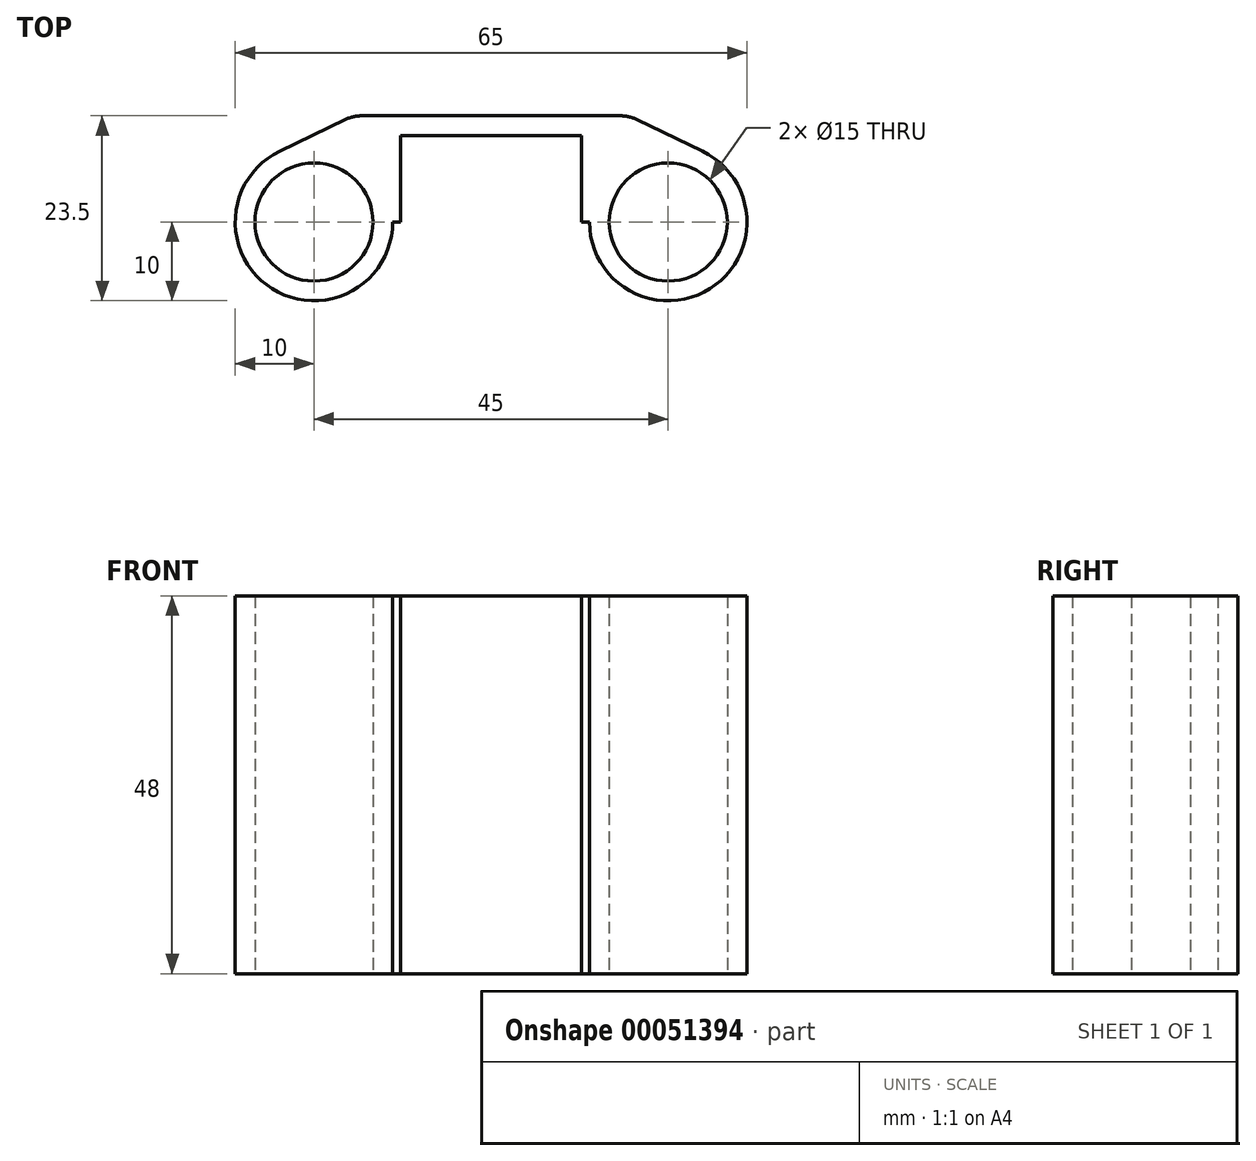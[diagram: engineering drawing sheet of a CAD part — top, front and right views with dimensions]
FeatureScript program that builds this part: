
annotation { "Feature Type Name" : "Feature", "Feature Type Description" : "" }
export const myFeature = defineFeature(function(context is Context, id is Id, definition is map)
    precondition{}
    {
        {
            var Q0;
            Q0=qCreatedBy(makeId("Top.planeOp"),FACE);
            var sketch = newSketch(context, id + "F0", { "sketchPlane" : qUnion([Q0])});
            skCircle(sketch, "E0", {"center": v(22.5, 0) * mm, "radius": 7.5 * mm});
            skCircle(sketch, "E1", {"center": v(-22.5, 0) * mm, "radius": 7.5 * mm});
            skLineSegment(sketch, "E2", {"start": v(-22.5, 0) * mm, "end": v(22.5, 0) * mm, "construction": true});
            skArc(sketch, "E3", {"start": v(-26.83, 9.01) * mm, "mid": v(-27.82, -8.47) * mm, "end": v(-12.5, 0) * mm});
            skArc(sketch, "E4", {"start": v(12.5, 0) * mm, "mid": v(27.82, -8.47) * mm, "end": v(26.83, 9.01) * mm});
            skLineSegment(sketch, "E5", {"start": v(0, 0) * mm, "end": v(0, 13.5) * mm, "construction": true});
            skLineSegment(sketch, "E6.bottom", {"start": v(10, 10) * mm, "end": v(-10, 10) * mm, "construction": true});
            skLineSegment(sketch, "E6.top", {"start": v(10, -10) * mm, "end": v(-10, -10) * mm, "construction": true});
            skLineSegment(sketch, "E6.left", {"start": v(10, 10) * mm, "end": v(10, -10) * mm, "construction": true});
            skLineSegment(sketch, "E6.right", {"start": v(-10, 10) * mm, "end": v(-10, -10) * mm, "construction": true});
            skPoint(sketch, "E6.middle", {"position": v(0, 0) * mm});
            skLineSegment(sketch, "E7", {"start": v(-22.5, 0) * mm, "end": v(-11.5, 11) * mm, "construction": true});
            skLineSegment(sketch, "E8", {"start": v(22.5, 0) * mm, "end": v(11.5, 11) * mm, "construction": true});
            skLineSegment(sketch, "E9", {"start": v(-11.5, 11) * mm, "end": v(11.5, 11) * mm});
            skLineSegment(sketch, "E10", {"start": v(-26.83, 9.01) * mm, "end": v(-17.5, 13.5) * mm});
            skLineSegment(sketch, "E11", {"start": v(-17.5, 13.5) * mm, "end": v(17.5, 13.5) * mm});
            skLineSegment(sketch, "E12", {"start": v(17.5, 13.5) * mm, "end": v(26.83, 9.01) * mm});
            skLineSegment(sketch, "E13", {"start": v(11.5, 11) * mm, "end": v(11.5, 0) * mm});
            skLineSegment(sketch, "E14", {"start": v(11.5, 0) * mm, "end": v(12.5, 0) * mm});
            skLineSegment(sketch, "E15", {"start": v(-11.5, 11) * mm, "end": v(-11.5, 0) * mm});
            skLineSegment(sketch, "E16", {"start": v(-11.5, 0) * mm, "end": v(-12.5, 0) * mm});
            skSolve(sketch);
        }
        {
            var Q0;
            Q0=makeQuery(id+"F0.imprint","IMPRINT",FACE,{"disambiguationData":[TD([[makeQuery(id+"F0.imprint","IMPRINT",EDGE,{"derivedFrom":sQuery(id+"F0.wireOp",EDGE,"E0")}),-1.0]])]});
            extrude(context, id + "F1", {"entities" : qUnion([Q0]), "endBound" : BoundingType.SYMMETRIC, "depth" : 48 * mm});
        }
        {
            var Q0;
            Q0=makeQuery(id+"F1.opExtrude","SWEPT_EDGE",EDGE,{"disambiguationData":[OSD([sQuery(id+"F0.wireOp",EDGE,"E11"),sQuery(id+"F0.wireOp",EDGE,"E12")])]});
            var Q1;
            Q1=makeQuery(id+"F1.opExtrude","SWEPT_EDGE",EDGE,{"disambiguationData":[OSD([sQuery(id+"F0.wireOp",EDGE,"E10"),sQuery(id+"F0.wireOp",EDGE,"E11")])]});
            fillet(context, id + "F2", {"entities" : qUnion([Q0, Q1]), "radius" : 5 * mm, "tangentPropagation" : true, "allowEdgeOverflow" : false});
        }
    });
